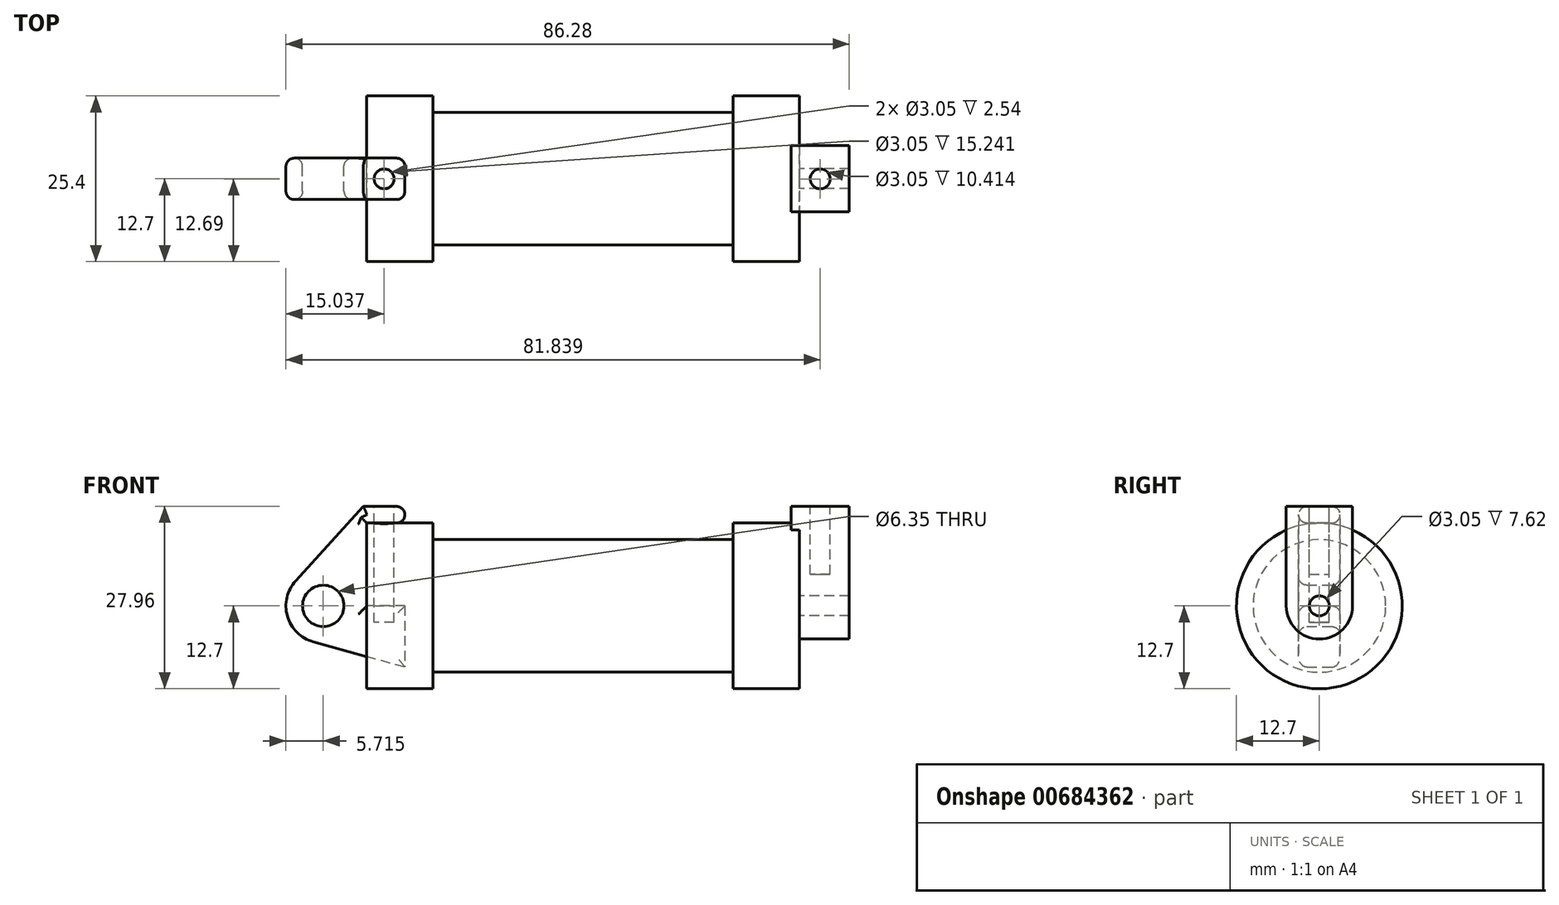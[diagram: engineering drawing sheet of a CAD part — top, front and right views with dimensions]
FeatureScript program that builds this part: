
annotation { "Feature Type Name" : "Feature", "Feature Type Description" : "" }
export const myFeature = defineFeature(function(context is Context, id is Id, definition is map)
    precondition{}
    {
        {
            var Q0;
            Q0=qCreatedBy(makeId("Front.planeOp"),FACE);
            var sketch = newSketch(context, id + "F0", { "sketchPlane" : qUnion([Q0])});
            skLineSegment(sketch, "E0", {"start": v(0, 0) * mm, "end": v(0, 12.7) * mm});
            skLineSegment(sketch, "E1", {"start": v(0, 12.7) * mm, "end": v(10.16, 12.7) * mm});
            skLineSegment(sketch, "E2", {"start": v(10.16, 12.7) * mm, "end": v(10.16, 10.16) * mm});
            skLineSegment(sketch, "E3", {"start": v(10.16, 10.16) * mm, "end": v(56.13, 10.16) * mm});
            skLineSegment(sketch, "E4", {"start": v(56.13, 10.16) * mm, "end": v(56.13, 12.7) * mm});
            skLineSegment(sketch, "E5", {"start": v(56.13, 12.7) * mm, "end": v(66.3, 12.7) * mm});
            skLineSegment(sketch, "E6", {"start": v(66.3, 12.7) * mm, "end": v(66.3, 0) * mm});
            skLineSegment(sketch, "E7", {"start": v(66.3, 0) * mm, "end": v(0, 0) * mm});
            skLineSegment(sketch, "E8", {"start": v(5.84, 15.24) * mm, "end": v(-0.5, 15.24) * mm});
            skLineSegment(sketch, "E9", {"start": v(-0.5, 15.24) * mm, "end": v(-10.88, 3.85) * mm});
            skLineSegment(sketch, "E10", {"start": v(0, 0) * mm, "end": v(-6.65, 0) * mm});
            skCircle(sketch, "E11", {"center": v(-6.65, 0) * mm, "radius": 5.72 * mm});
            skCircle(sketch, "E12", {"center": v(-6.65, 0) * mm, "radius": 3.18 * mm});
            skLineSegment(sketch, "E13", {"start": v(5.84, 15.24) * mm, "end": v(5.84, -9.4) * mm});
            skLineSegment(sketch, "E14", {"start": v(5.84, -9.4) * mm, "end": v(-8.18, -5.5) * mm});
            skText(sketch, "E15", { "text": "1.721 in3 Sosa", "fontName": "OpenSans-Regular.ttf"});
            const initialGuessF0  = {"E15": [-0.04425, 0.0345, 1, 0, 0.01433]};
            skSetInitialGuess(sketch, initialGuessF0);
            skSolve(sketch);
        }
        {
            var Q0;
            {var subQ0=sQuery(id+"F0.wireOp",EDGE,"E0");Q0=makeQuery(id+"F0.imprint","IMPRINT",FACE,{"disambiguationData":[TD([[makeQuery(id+"F0.imprint","IMPRINT",EDGE,{"derivedFrom":subQ0}),-1.0]])]});}
            var Q1;
            {var subQ0=sQuery(id+"F0.wireOp",EDGE,"E2");Q1=makeQuery(id+"F0.imprint","IMPRINT",FACE,{"disambiguationData":[TD([[makeQuery(id+"F0.imprint","IMPRINT",EDGE,{"derivedFrom":subQ0}),-1.0]])]});}
            var Q2;
            Q2=sQuery(id+"F0.wireOp",EDGE,"E7");
            revolve(context, id + "F1", {"entities" : qUnion([Q0, Q1]), "axis" : qUnion([Q2]), "revolveType" : RevolveType.FULL});
        }
        {
            var Q0;
            {var subQ1=sQuery(id+"F0.wireOp",EDGE,"E0");Q0=makeQuery(id+"F0.imprint","IMPRINT",FACE,{"disambiguationData":[TD([[makeQuery(id+"F0.imprint","IMPRINT",EDGE,{"derivedFrom":subQ1}),1.0]])]});}
            var Q1;
            {var subQ5=sQuery(id+"F0.wireOp",EDGE,"E12");Q1=makeQuery(id+"F0.imprint","IMPRINT",FACE,{"disambiguationData":[TD([[makeQuery(id+"F0.imprint","IMPRINT",EDGE,{"derivedFrom":subQ5}),-1.0]])]});}
            var Q2;
            {var subQ0=sQuery(id+"F0.wireOp",EDGE,"E14");Q2=makeQuery(id+"F0.imprint","IMPRINT",FACE,{"disambiguationData":[TD([[makeQuery(id+"F0.imprint","IMPRINT",EDGE,{"derivedFrom":subQ0}),-1.0]])]});}
            extrude(context, id + "F2", {"entities" : qUnion([Q0, Q1, Q2]), "endBound" : BoundingType.SYMMETRIC, "depth" : 6.35 * mm, "offsetDistance" : 25.4 * mm});
        }
        {
            var Q0;
            Q0=makeQuery(id+"F1.opRevolve","SWEPT_FACE",FACE,{"disambiguationData":[OSD([sQuery(id+"F0.wireOp",EDGE,"E6")])]});
            var sketch = newSketch(context, id + "F3", { "sketchPlane" : qUnion([Q0])});
            skCircle(sketch, "E16", {"center": v(0, 0) * mm, "radius": 1.52 * mm});
            skCircle(sketch, "E17", {"center": v(0, 0) * mm, "radius": 5.08 * mm});
            skLineSegment(sketch, "E18", {"start": v(-5.08, 0) * mm, "end": v(-5.08, 15.26) * mm});
            skLineSegment(sketch, "E19", {"start": v(5.08, 0) * mm, "end": v(5.08, 15.24) * mm});
            skLineSegment(sketch, "E20", {"start": v(5.08, 15.24) * mm, "end": v(-5.08, 15.26) * mm});
            skSolve(sketch);
        }
        {
            var Q0;
            Q0=makeQuery(id+"F3.imprint","IMPRINT",FACE,{"disambiguationData":[TD([[makeQuery(id+"F3.imprint","IMPRINT",EDGE,{"derivedFrom":sQuery(id+"F3.wireOp",EDGE,"E16")}),-1.0]])]});
            var Q1;
            {var subQ0=sQuery(id+"F3.wireOp",EDGE,"E20");Q1=makeQuery(id+"F3.imprint","IMPRINT",FACE,{"disambiguationData":[TD([[makeQuery(id+"F3.imprint","IMPRINT",EDGE,{"derivedFrom":subQ0}),1.0]])]});}
            var Q2;
            {var subQ0=sQuery(id+"F3.wireOp",EDGE,"E18");var subQ1=sQuery(id+"F3.wireOp",EDGE,"E17");var subQ2=makeQuery(id+"F3.imprint","INTERSECT",VERTEX,{"derivedFrom":[subQ1,subQ0]});Q2=makeQuery(id+"F3.imprint","IMPRINT",FACE,{"disambiguationData":[TD([[makeQuery(id+"F3.imprint","IMPRINT",EDGE,{"disambiguationData":[TD([[subQ2,1.0]])],"derivedFrom":subQ1}),-1.0]])]});}
            extrude(context, id + "F4", {"entities" : qUnion([Q0, Q1, Q2]), "operationType" : NewBodyOperationType.ADD, "depth" : 7.62 * mm, "offsetDistance" : 25.4 * mm, "hasSecondDirection" : true, "secondDirectionOppositeDirection" : true, "secondDirectionDepth" : 1.27 * mm});
        }
        {
            var Q0;
            Q0=makeQuery(id+"F2.opExtrude","SWEPT_FACE",FACE,{"disambiguationData":[OSD([sQuery(id+"F0.wireOp",EDGE,"E8")])]});
            var sketch = newSketch(context, id + "F5", { "sketchPlane" : qUnion([Q0])});
            skLineSegment(sketch, "E21", {"start": v(-0.5, 3.18) * mm, "end": v(5.84, -3.18) * mm, "construction": true});
            skCircle(sketch, "E22", {"center": v(2.67, 0) * mm, "radius": 1.52 * mm});
            skSolve(sketch);
        }
        {
            var Q0;
            Q0=makeQuery(id+"F4.opExtrude","SWEPT_FACE",FACE,{"disambiguationData":[OSD([sQuery(id+"F3.wireOp",EDGE,"E20")])]});
            var sketch = newSketch(context, id + "F6", { "sketchPlane" : qUnion([Q0])});
            skLineSegment(sketch, "E23", {"start": v(65.02, 5.05) * mm, "end": v(73.91, -5.11) * mm, "construction": true});
            skCircle(sketch, "E24", {"center": v(69.47, -0.03) * mm, "radius": 1.52 * mm});
            skSolve(sketch);
        }
        {
            var Q0;
            Q0=makeQuery(id+"F5.imprint","IMPRINT",FACE,{"disambiguationData":[TD([[makeQuery(id+"F5.imprint","IMPRINT",EDGE,{"derivedFrom":sQuery(id+"F5.wireOp",EDGE,"E22")}),1.0]])]});
            extrude(context, id + "F7", {"entities" : qUnion([Q0]), "operationType" : NewBodyOperationType.REMOVE, "oppositeDirection" : true, "depth" : 17.78 * mm, "offsetDistance" : 25.4 * mm});
        }
        {
            var Q0;
            Q0=makeQuery(id+"F6.imprint","IMPRINT",FACE,{"disambiguationData":[TD([[makeQuery(id+"F6.imprint","IMPRINT",EDGE,{"derivedFrom":sQuery(id+"F6.wireOp",EDGE,"E24")}),1.0]])]});
            extrude(context, id + "F8", {"entities" : qUnion([Q0]), "operationType" : NewBodyOperationType.REMOVE, "oppositeDirection" : true, "depth" : 10.4 * mm, "offsetDistance" : 25.4 * mm});
        }
        {
            var Q0;
            Q0=makeQuery(id+"F1.opRevolve","SWEPT_EDGE",EDGE,{"disambiguationData":[OSD([sQuery(id+"F0.wireOp",EDGE,"E1"),sQuery(id+"F0.wireOp",EDGE,"E2")])]});
            var Q1;
            Q1=makeQuery(id+"F1.opRevolve","SWEPT_EDGE",EDGE,{"disambiguationData":[OSD([sQuery(id+"F0.wireOp",EDGE,"E0"),sQuery(id+"F0.wireOp",EDGE,"E1")])]});
            var Q2;
            Q2=makeQuery(id+"F1.opRevolve","SWEPT_EDGE",EDGE,{"disambiguationData":[OSD([sQuery(id+"F0.wireOp",EDGE,"E4"),sQuery(id+"F0.wireOp",EDGE,"E5")])]});
            var Q3;
            Q3=makeQuery(id+"F1.opRevolve","SWEPT_EDGE",EDGE,{"disambiguationData":[OSD([sQuery(id+"F0.wireOp",EDGE,"E5"),sQuery(id+"F0.wireOp",EDGE,"E6")])]});
            var Q4;
            Q4=makeQuery(id+"F4.opExtrude","CAP_FACE",FACE,{"disambiguationData":[OSD([sQuery(id+"F3.wireOp",EDGE,"E16"),sQuery(id+"F3.wireOp",EDGE,"E17"),sQuery(id+"F3.wireOp",EDGE,"E18"),sQuery(id+"F3.wireOp",EDGE,"E19"),sQuery(id+"F3.wireOp",EDGE,"E20")])],"isStart":true});
            var Q5;
            Q5=makeQuery(id+"F4.opExtrude","SWEPT_EDGE",EDGE,{"disambiguationData":[OSD([sQuery(id+"F3.wireOp",EDGE,"E18"),sQuery(id+"F3.wireOp",EDGE,"E20")])]});
            var Q6;
            Q6=makeQuery(id+"F4.opExtrude","CAP_FACE",FACE,{"disambiguationData":[OSD([sQuery(id+"F3.wireOp",EDGE,"E16"),sQuery(id+"F3.wireOp",EDGE,"E17"),sQuery(id+"F3.wireOp",EDGE,"E18"),sQuery(id+"F3.wireOp",EDGE,"E19"),sQuery(id+"F3.wireOp",EDGE,"E20")])],"isStart":false});
            var Q7;
            Q7=makeQuery(id+"F2.opExtrude","CAP_EDGE",EDGE,{"disambiguationData":[OSD([sQuery(id+"F0.wireOp",EDGE,"E9")])],"isStart":false});
            var Q8;
            Q8=makeQuery(id+"F2.opExtrude","SWEPT_FACE",FACE,{"disambiguationData":[OSD([sQuery(id+"F0.wireOp",EDGE,"E11")])]});
            var Q9;
            Q9=makeQuery(id+"F2.opExtrude","CAP_FACE",FACE,{"disambiguationData":[OSD([sQuery(id+"F0.wireOp",EDGE,"E0"),sQuery(id+"F0.wireOp",EDGE,"E1"),sQuery(id+"F0.wireOp",EDGE,"E7"),sQuery(id+"F0.wireOp",EDGE,"E8"),sQuery(id+"F0.wireOp",EDGE,"E9"),sQuery(id+"F0.wireOp",EDGE,"E11"),sQuery(id+"F0.wireOp",EDGE,"E12"),sQuery(id+"F0.wireOp",EDGE,"E13"),sQuery(id+"F0.wireOp",EDGE,"E14")])],"isStart":false});
            var Q10;
            {var subQ0=sQuery(id+"F0.wireOp",EDGE,"E13");Q10=makeQuery(id+"F2.opExtrude","SWEPT_FACE",FACE,{"disambiguationData":[OSD([subQ0]),TDD([makeQuery(id+"F0.imprint","IMPRINT",EDGE,{"disambiguationData":[TD([[makeQuery(id+"F0.imprint","INTERSECT",VERTEX,{"derivedFrom":[sQuery(id+"F0.wireOp",EDGE,"E8"),subQ0]}),-1.0]])],"derivedFrom":subQ0})])]});}
            var Q11;
            Q11=makeQuery(id+"F2.opExtrude","CAP_FACE",FACE,{"disambiguationData":[OSD([sQuery(id+"F0.wireOp",EDGE,"E0"),sQuery(id+"F0.wireOp",EDGE,"E1"),sQuery(id+"F0.wireOp",EDGE,"E7"),sQuery(id+"F0.wireOp",EDGE,"E8"),sQuery(id+"F0.wireOp",EDGE,"E9"),sQuery(id+"F0.wireOp",EDGE,"E11"),sQuery(id+"F0.wireOp",EDGE,"E12"),sQuery(id+"F0.wireOp",EDGE,"E13"),sQuery(id+"F0.wireOp",EDGE,"E14")])],"isStart":true});
            fillet(context, id + "F9", {"entities" : qUnion([Q0, Q1, Q2, Q3, Q4, Q5, Q6, Q7, Q8, Q9, Q10, Q11]), "radius" : 1.27 * mm, "tangentPropagation" : true, "allowEdgeOverflow" : false});
        }
    });
